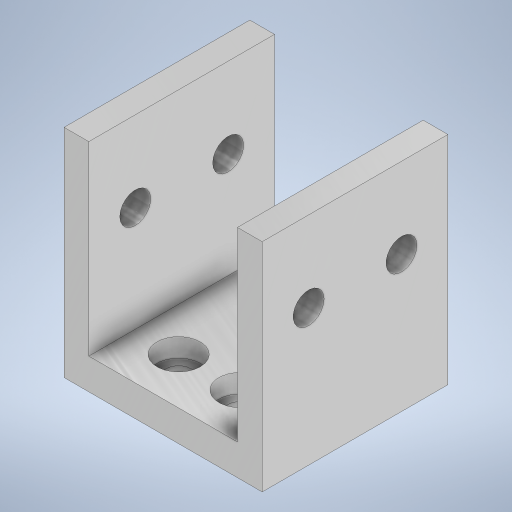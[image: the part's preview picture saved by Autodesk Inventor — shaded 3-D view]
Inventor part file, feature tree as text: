
AUTODESK INVENTOR PART (.ipt)
format: ipt  version: 2023.2 (Build 272271030, 271C)  size: 286,208 bytes
history: native  units: mm
features: sketch x4, extrude x2, hole x2
ambient origin geometry x8: Origin, YZ Plane, XZ Plane, XY Plane, X Axis, Y Axis, Z Axis, Center Point
bodies: Solid2 (feature_tree)
feature tree (8):
  extrude  "Extrusion1"  Depth=30.0mm
  extrude  "Extrusion2"  Depth=4.0mm
  hole  "Hole2"  [1 undecoded]
  hole  "Furo3"  [1 undecoded]
  sketch  "Esboço1"  dims[d0=32.0mm d1=30.0mm]
  sketch  "Sketch4"  dims[d24=5.0mm d25=0.0mm d26=4.0mm]
  sketch  "Sketch5"  dims[d27=4.0mm d28=30.0mm d29=0.0mm]
  sketch  "Esboço6"  dims[d30=7.5mm d31=7.5mm d32=13.0mm d33=13.0mm d34=5.0mm d35=6.0mm d36=4.0mm d37=2.0mm d38=90.0deg d39=5.0mm d40=20.594885mm d41=10.0mm d42=10.0mm d43=15.0mm d44=15.0mm d45=24.0mm d46=7.0mm d47=0.0mm d48=30.0mm d49=7.5mm d50=4.0mm d51=6.0mm d52=7.0mm d53=3.0mm d54=90.0deg d55=5.0mm d56=20.594885mm]
note: 2 required parameter values undecoded (feature->parameter linkage not recoverable at this tier; creation-order binding heuristic only, values carry confidence <= 0.55)
